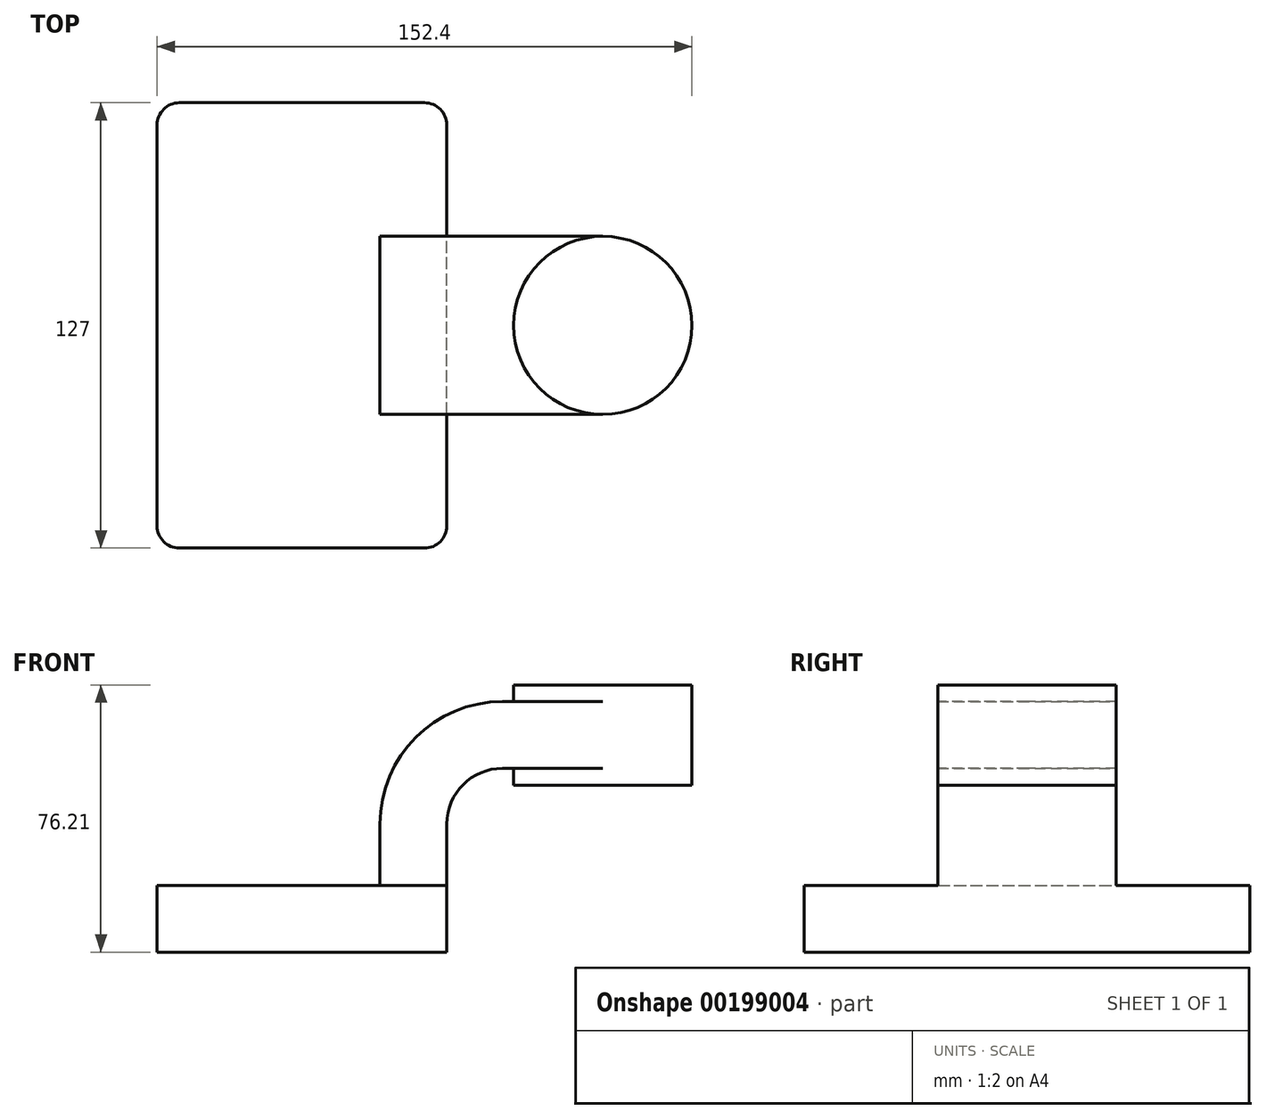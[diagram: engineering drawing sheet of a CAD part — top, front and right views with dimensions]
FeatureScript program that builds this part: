
annotation { "Feature Type Name" : "Feature", "Feature Type Description" : "" }
export const myFeature = defineFeature(function(context is Context, id is Id, definition is map)
    precondition{}
    {
        {
            var Q0;
            Q0=qCreatedBy(makeId("Front.planeOp"),FACE);
            var sketch = newSketch(context, id + "F0", { "sketchPlane" : qUnion([Q0])});
            skLineSegment(sketch, "E0.bottom", {"start": v(41.27, 9.53) * mm, "end": v(-41.28, 9.53) * mm});
            skLineSegment(sketch, "E0.top", {"start": v(41.28, -9.52) * mm, "end": v(-41.27, -9.52) * mm});
            skLineSegment(sketch, "E0.left", {"start": v(41.28, 9.53) * mm, "end": v(41.28, -9.52) * mm});
            skLineSegment(sketch, "E0.right", {"start": v(-41.28, 9.53) * mm, "end": v(-41.27, -9.52) * mm});
            skPoint(sketch, "E0.middle", {"position": v(0, 0) * mm});
            skLineSegment(sketch, "E1.bottom", {"start": v(60.33, 38.1) * mm, "end": v(111.13, 38.1) * mm});
            skLineSegment(sketch, "E1.top", {"start": v(60.33, 66.68) * mm, "end": v(111.13, 66.68) * mm});
            skLineSegment(sketch, "E1.left", {"start": v(60.33, 38.1) * mm, "end": v(60.33, 66.68) * mm});
            skLineSegment(sketch, "E1.right", {"start": v(111.13, 38.1) * mm, "end": v(111.13, 66.68) * mm});
            skPoint(sketch, "E1.middle", {"position": v(85.73, 52.39) * mm});
            skLineSegment(sketch, "E2", {"start": v(41.27, 9.53) * mm, "end": v(41.27, 27) * mm});
            skArc(sketch, "E3", {"start": v(41.27, 27) * mm, "mid": v(45.92, 38.23) * mm, "end": v(57.15, 42.88) * mm});
            skLineSegment(sketch, "E4", {"start": v(57.15, 42.88) * mm, "end": v(85.73, 42.88) * mm});
            skLineSegment(sketch, "E5.0", {"start": v(57.15, 61.93) * mm, "end": v(85.73, 61.93) * mm});
            skArc(sketch, "E5.1", {"start": v(22.23, 27) * mm, "mid": v(32.45, 51.7) * mm, "end": v(57.15, 61.93) * mm});
            skLineSegment(sketch, "E5.2", {"start": v(22.22, 9.53) * mm, "end": v(22.22, 27) * mm});
            skLineSegment(sketch, "E6", {"start": v(85.73, 35.96) * mm, "end": v(85.73, 66.68) * mm});
            skPoint(sketch, "E6.startSnap0", {"position": v(85.73, 38.1) * mm});
            skFitSpline(sketch, "E7", {"points": [v(-41.28, 9.52) * mm, v(57.15, 61.93) * mm], "startDerivative": vector(-0.14, 96.51) * mm, "endDerivative": vector(92.4, -1.76) * mm});
            skSolve(sketch);
        }
        {
            var Q0;
            Q0=makeQuery(id+"F0.imprint","IMPRINT",FACE,{"disambiguationData":[TD([[makeQuery(id+"F0.imprint","IMPRINT",EDGE,{"derivedFrom":sQuery(id+"F0.wireOp",EDGE,"E0.top")}),-1.0]])]});
            extrude(context, id + "F1", {"entities" : qUnion([Q0]), "endBound" : BoundingType.SYMMETRIC, "depth" : 127 * mm});
        }
        {
            var Q0;
            {var subQ1=sQuery(id+"F0.wireOp",EDGE,"E2");Q0=makeQuery(id+"F0.imprint","IMPRINT",FACE,{"disambiguationData":[TD([[makeQuery(id+"F0.imprint","IMPRINT",EDGE,{"derivedFrom":subQ1}),1.0]])]});}
            var Q1;
            {var subQ0=sQuery(id+"F0.wireOp",EDGE,"E4");var subQ1=sQuery(id+"F0.wireOp",EDGE,"E1.left");var subQ2=makeQuery(id+"F0.imprint","INTERSECT",VERTEX,{"derivedFrom":[subQ1,subQ0]});Q1=makeQuery(id+"F0.imprint","IMPRINT",FACE,{"disambiguationData":[TD([[makeQuery(id+"F0.imprint","IMPRINT",EDGE,{"disambiguationData":[TD([[subQ2,-1.0]])],"derivedFrom":subQ1}),-1.0]])]});}
            extrude(context, id + "F2", {"entities" : qUnion([Q0, Q1]), "operationType" : NewBodyOperationType.ADD, "endBound" : BoundingType.SYMMETRIC, "depth" : 50.8 * mm});
        }
        {
            var Q0;
            Q0=makeQuery(id+"F0.imprint","IMPRINT",FACE,{"disambiguationData":[TD([[makeQuery(id+"F0.imprint","IMPRINT",EDGE,{"derivedFrom":sQuery(id+"F0.wireOp",EDGE,"E5.1")}),1.0]])]});
            extrude(context, id + "F3", {"entities" : qUnion([Q0]), "operationType" : NewBodyOperationType.ADD, "endBound" : BoundingType.SYMMETRIC, "depth" : 15.88 * mm});
        }
        {
            var Q0;
            {var subQ0=sQuery(id+"F0.wireOp",EDGE,"E1.right");Q0=makeQuery(id+"F0.imprint","IMPRINT",FACE,{"disambiguationData":[TD([[makeQuery(id+"F0.imprint","IMPRINT",EDGE,{"derivedFrom":subQ0}),1.0]])]});}
            var Q1;
            Q1=sQuery(id+"F0.wireOp",EDGE,"E6");
            revolve(context, id + "F4", {"operationType" : NewBodyOperationType.ADD, "entities" : qUnion([Q0]), "axis" : qUnion([Q1]), "revolveType" : RevolveType.FULL});
        }
        {
            var Q0;
            Q0=makeQuery(id+"F1.opExtrude","CAP_EDGE",EDGE,{"disambiguationData":[OSD([sQuery(id+"F0.wireOp",EDGE,"E0.left")])],"isStart":false});
            var Q1;
            Q1=makeQuery(id+"F1.opExtrude","CAP_EDGE",EDGE,{"disambiguationData":[OSD([sQuery(id+"F0.wireOp",EDGE,"E0.right")])],"isStart":false});
            var Q2;
            Q2=makeQuery(id+"F1.opExtrude","CAP_EDGE",EDGE,{"disambiguationData":[OSD([sQuery(id+"F0.wireOp",EDGE,"E0.right")])],"isStart":true});
            var Q3;
            Q3=makeQuery(id+"F1.opExtrude","CAP_EDGE",EDGE,{"disambiguationData":[OSD([sQuery(id+"F0.wireOp",EDGE,"E0.left")])],"isStart":true});
            fillet(context, id + "F5", {"entities" : qUnion([Q0, Q1, Q2, Q3]), "radius" : 6.35 * mm, "tangentPropagation" : true, "allowEdgeOverflow" : false});
        }
    });
